# Revit family: Lighting_Pendant-Lighting_Molto-Luce_Log-Out-2-1-Bina-Recessed_999
name_source: partatom
category: Lighting Fixtures
revit_build: Autodesk Revit 2018 (Build: 20170223_1515(x64)
units: mm (PartAtom-declared; Revit-internal decimal feet)

## family parameters
Cut with Voids When Loaded = No
Host = Face
Light Source = Yes
OmniClass Number = 23.80.70.00
OmniClass Title = Lighting
Part Type = Normal
Room Calculation Point = No
Round Connector Dimension = Use Diameter
Shared = No

## types (1)
- Default - please load Revit Family Type Catalog
    BIMobject category = Pendant Lighting
    Color Filter = 16777215
    Decor Color = Molto Luce - White
    Default Elevation = 1219 mm
    Description = LOG OUT 2.1 & LOG IN 2.1 are available as pendant, surface-mounted and recessed luminaires. The profile is made of extruded aluminium and is available in black, white and aluminium-coloured surfaces. Due to its simple, straightforward look, the LOG series can be integrated discretely, yet distinctively into any style of architecture as a great lighting solution. The modular system offers additional components which can be perfectly combined with the profile. The lighting inserts with opal cover or microprismatic foil as well as the new BINA inserts which are available as UGR<19 and as ball-proof version, are just perfect as basic lighting. The Trigga insert and the MOVA spotlight can be used as additional lighting elements for the LOG OUT 2.1, LOG IN 2.1 & LOG IN TRIMLESS 2.1 system.
    Design country = Austria
    Dimming Lamp Color Temperature Shift = <None>
    Edition number = 1
    Emit from Line Length = 4220 mm  [stored 13.8451 ft]
    Housing Color = Molto Luce - Black
    IFC Classification = Lamp
    Installation instructions = https://www.moltoluce.com
    Length 1131 mm = No
    Length 1411 mm = No
    Length 2255 mm = No
    Length 2816 mm = No
    Length 3379 mm = No
    Length 4220 mm = Yes
    Light Location = 2092 mm
    Light Source Symbol Size = 610 mm
    Manufacturer = Molto Luce
    Manufacturer country = Austria
    Manufacturer name = Molto Luce
    Masterformat 2014 Code = 26 50 00
    Masterformat 2014 Description = Lighting
    Material main = Aluminium
    Material secondary = Acrylic
    Model = Log Out 2.1 Bina Recessed
    NBS Reference Code = 49
    NBS Reference Description = Luminaires And Lamps
    OmniClass Code = 23-35 45 15
    OmniClass Description = Lamps
    Product Guid = 5c26f14e-2a32-4198-a6b0-4133399f2653
    Product SKU = Log_Out_2_1_Bina_Recessed
    Product data url = https://bimobject.com
    Product family = Lighting
    Product group = Pendant Lamp
    Product name = Log Out 2.1 Bina Recessed
    Product url = https://www.moltoluce.com
    QR code = https://bimobject.com
    UNSPSC Code = 3911
    URL = https://www.moltoluce.com
    Uniclass 1.4 Code = JY73
    Uniclass 1.4 Description = Luminaires and lamps
    Uniclass 2.0 Code = PR-49
    Uniclass 2.0 Description = Luminaires And Lamps
    Uniclass 2015 Code = Pr_70_70_48
    Uniclass 2015 Name = Luminaires, lighting track and lighting accessories
    Uniformat II Code = D5020
    Uniformat II Description = Lighting & Branch Wiring

note: [stored X ft] marks values corroborated as IEEE doubles in the binary element streams (Revit-internal decimal feet)

## geometry (parser evidence)
native form markers: Sweep x5
no freeform markers — native parametric forms only
